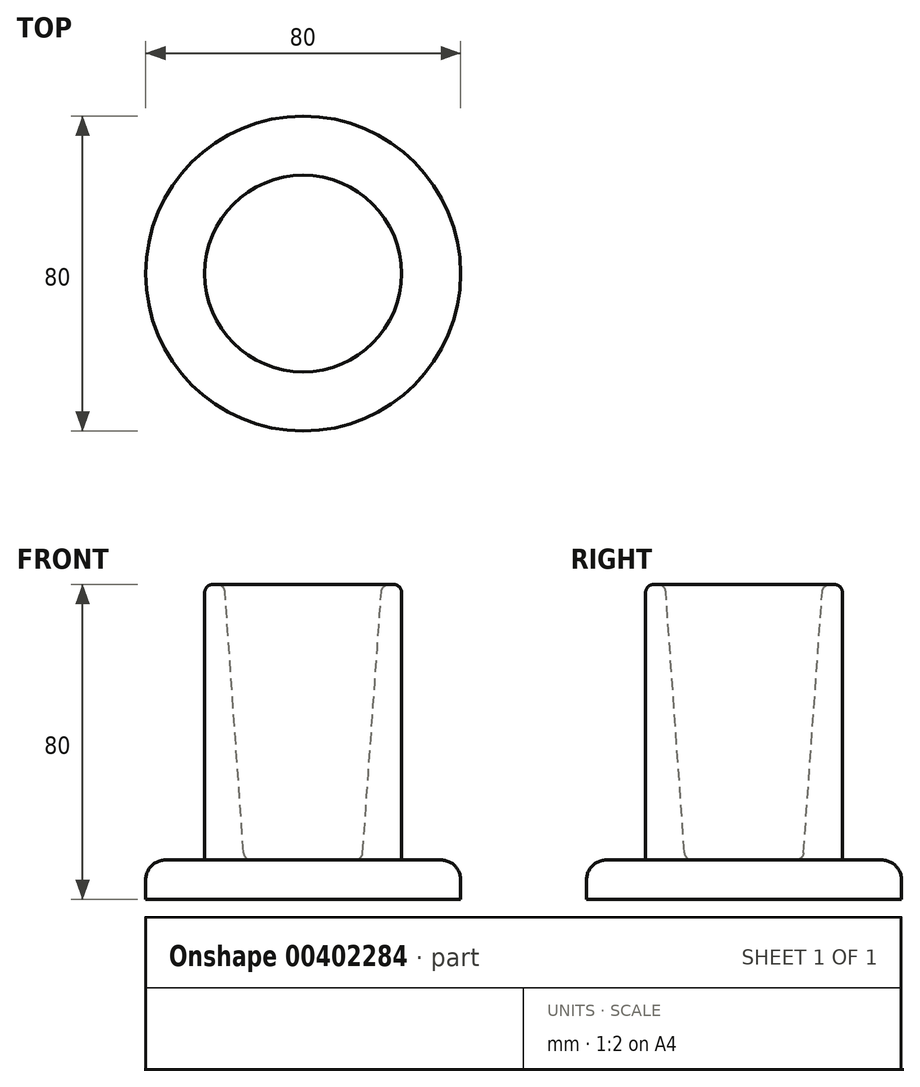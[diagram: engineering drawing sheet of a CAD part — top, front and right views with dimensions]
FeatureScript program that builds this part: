
annotation { "Feature Type Name" : "Feature", "Feature Type Description" : "" }
export const myFeature = defineFeature(function(context is Context, id is Id, definition is map)
    precondition{}
    {
        {
            var Q0;
            Q0=qCreatedBy(makeId("Front.planeOp"),FACE);
            var sketch = newSketch(context, id + "F0", { "sketchPlane" : qUnion([Q0])});
            skLineSegment(sketch, "E0", {"start": v(0, 0) * mm, "end": v(-40, 0) * mm});
            skLineSegment(sketch, "E1", {"start": v(-40, 0) * mm, "end": v(-40, 10) * mm});
            skLineSegment(sketch, "E2", {"start": v(-40, 10) * mm, "end": v(-25, 10) * mm});
            skLineSegment(sketch, "E3", {"start": v(-25, 10) * mm, "end": v(-25, 80) * mm});
            skLineSegment(sketch, "E4", {"start": v(-25, 80) * mm, "end": v(-20, 80) * mm});
            skLineSegment(sketch, "E5", {"start": v(0, 10) * mm, "end": v(0, 0) * mm});
            skLineSegment(sketch, "E6", {"start": v(0, 10) * mm, "end": v(-15, 10) * mm});
            skLineSegment(sketch, "E7", {"start": v(-15, 10) * mm, "end": v(-20, 80) * mm});
            skLineSegment(sketch, "E8", {"start": v(0, 0) * mm, "end": v(0, 123.06) * mm, "construction": true});
            skSolve(sketch);
        }
        {
            var Q0;
            Q0=makeQuery(id+"F0.imprint","IMPRINT",FACE,{"disambiguationData":[TD([[makeQuery(id+"F0.imprint","IMPRINT",EDGE,{"derivedFrom":sQuery(id+"F0.wireOp",EDGE,"E0")}),-1.0]])]});
            var Q1;
            Q1=sQuery(id+"F0.wireOp",EDGE,"E5");
            revolve(context, id + "F1", {"entities" : qUnion([Q0]), "axis" : qUnion([Q1]), "revolveType" : RevolveType.FULL});
        }
        {
            var Q0;
            Q0=makeQuery(id+"F1.opRevolve","SWEPT_EDGE",EDGE,{"disambiguationData":[OSD([sQuery(id+"F0.wireOp",EDGE,"E6"),sQuery(id+"F0.wireOp",EDGE,"E7")])]});
            var Q1;
            Q1=makeQuery(id+"F1.opRevolve","SWEPT_EDGE",EDGE,{"disambiguationData":[OSD([sQuery(id+"F0.wireOp",EDGE,"E4"),sQuery(id+"F0.wireOp",EDGE,"E7")])]});
            var Q2;
            Q2=makeQuery(id+"F1.opRevolve","SWEPT_EDGE",EDGE,{"disambiguationData":[OSD([sQuery(id+"F0.wireOp",EDGE,"E3"),sQuery(id+"F0.wireOp",EDGE,"E4")])]});
            fillet(context, id + "F2", {"entities" : qUnion([Q0, Q1, Q2]), "radius" : 2 * mm, "tangentPropagation" : true, "allowEdgeOverflow" : false});
        }
        {
            var Q0;
            Q0=makeQuery(id+"F1.opRevolve","SWEPT_EDGE",EDGE,{"disambiguationData":[OSD([sQuery(id+"F0.wireOp",EDGE,"E1"),sQuery(id+"F0.wireOp",EDGE,"E2")])]});
            fillet(context, id + "F3", {"entities" : qUnion([Q0]), "radius" : 5 * mm, "tangentPropagation" : true, "allowEdgeOverflow" : false});
        }
    });
